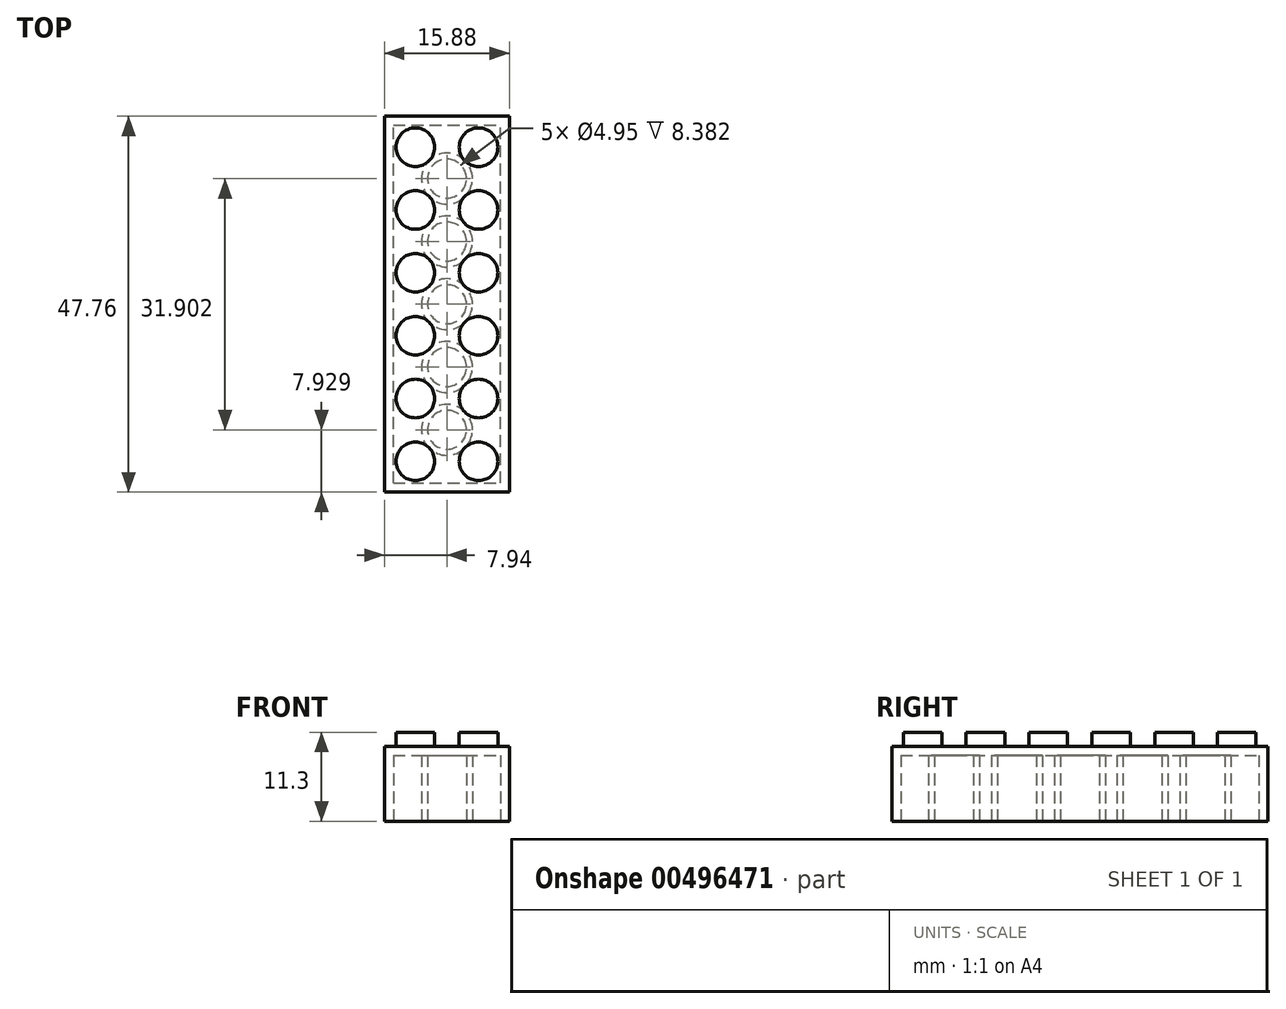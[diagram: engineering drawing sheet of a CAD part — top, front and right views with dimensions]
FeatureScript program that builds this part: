
annotation { "Feature Type Name" : "Feature", "Feature Type Description" : "" }
export const myFeature = defineFeature(function(context is Context, id is Id, definition is map)
    precondition{}
    {
        {
            var Q0;
            Q0=qCreatedBy(makeId("Top.planeOp"),FACE);
            var sketch = newSketch(context, id + "F0", { "sketchPlane" : qUnion([Q0])});
            skLineSegment(sketch, "E0.bottom", {"start": v(7.94, 23.88) * mm, "end": v(-7.94, 23.88) * mm});
            skLineSegment(sketch, "E0.top", {"start": v(7.94, -23.88) * mm, "end": v(-7.94, -23.88) * mm});
            skLineSegment(sketch, "E0.left", {"start": v(7.94, 23.88) * mm, "end": v(7.94, -23.88) * mm});
            skLineSegment(sketch, "E0.right", {"start": v(-7.94, 23.88) * mm, "end": v(-7.94, -23.88) * mm});
            skPoint(sketch, "E0.middle", {"position": v(0, 0) * mm});
            skSolve(sketch);
        }
        {
            var Q0;
            Q0=makeQuery(id+"F0.imprint","IMPRINT",FACE,{"disambiguationData":[TD([[makeQuery(id+"F0.imprint","IMPRINT",EDGE,{"derivedFrom":sQuery(id+"F0.wireOp",EDGE,"E0.bottom")}),1.0]])]});
            extrude(context, id + "F1", {"entities" : qUnion([Q0]), "endBound" : BoundingType.SYMMETRIC, "depth" : 9.52 * mm});
        }
        {
            var Q0;
            Q0=makeQuery(id+"F1.opExtrude","CAP_FACE",FACE,{"disambiguationData":[OSD([sQuery(id+"F0.wireOp",EDGE,"E0.bottom"),sQuery(id+"F0.wireOp",EDGE,"E0.top"),sQuery(id+"F0.wireOp",EDGE,"E0.left"),sQuery(id+"F0.wireOp",EDGE,"E0.right")])],"isStart":false});
            var sketch = newSketch(context, id + "F2", { "sketchPlane" : qUnion([Q0])});
            skCircle(sketch, "E1", {"center": v(-4.01, 19.95) * mm, "radius": 2.45 * mm});
            skCircle(sketch, "E2", {"center": v(4.01, 19.95) * mm, "radius": 2.45 * mm});
            skCircle(sketch, "E3", {"center": v(-4.01, -19.95) * mm, "radius": 2.45 * mm});
            skCircle(sketch, "E4", {"center": v(4.01, -19.95) * mm, "radius": 2.45 * mm});
            skCircle(sketch, "E5", {"center": v(4.01, -11.98) * mm, "radius": 2.45 * mm});
            skCircle(sketch, "E6", {"center": v(4.01, -4) * mm, "radius": 2.45 * mm});
            skCircle(sketch, "E7", {"center": v(-4.01, -11.98) * mm, "radius": 2.45 * mm});
            skCircle(sketch, "E8", {"center": v(-4.01, -4) * mm, "radius": 2.45 * mm});
            skCircle(sketch, "E9", {"center": v(-4.01, 11.98) * mm, "radius": 2.45 * mm});
            skCircle(sketch, "E10", {"center": v(4.01, 11.98) * mm, "radius": 2.45 * mm});
            skCircle(sketch, "E11", {"center": v(4.01, 4) * mm, "radius": 2.45 * mm});
            skCircle(sketch, "E12", {"center": v(-4.01, 4) * mm, "radius": 2.45 * mm});
            skSolve(sketch);
        }
        {
            var Q0;
            Q0=makeQuery(id+"F2.imprint","IMPRINT",FACE,{"disambiguationData":[TD([[makeQuery(id+"F2.imprint","IMPRINT",EDGE,{"derivedFrom":sQuery(id+"F2.wireOp",EDGE,"E1")}),1.0]])]});
            var Q1;
            Q1=makeQuery(id+"F2.imprint","IMPRINT",FACE,{"disambiguationData":[TD([[makeQuery(id+"F2.imprint","IMPRINT",EDGE,{"derivedFrom":sQuery(id+"F2.wireOp",EDGE,"E2")}),1.0]])]});
            var Q2;
            Q2=makeQuery(id+"F2.imprint","IMPRINT",FACE,{"disambiguationData":[TD([[makeQuery(id+"F2.imprint","IMPRINT",EDGE,{"derivedFrom":sQuery(id+"F2.wireOp",EDGE,"E9")}),1.0]])]});
            var Q3;
            Q3=makeQuery(id+"F2.imprint","IMPRINT",FACE,{"disambiguationData":[TD([[makeQuery(id+"F2.imprint","IMPRINT",EDGE,{"derivedFrom":sQuery(id+"F2.wireOp",EDGE,"E10")}),1.0]])]});
            var Q4;
            Q4=makeQuery(id+"F2.imprint","IMPRINT",FACE,{"disambiguationData":[TD([[makeQuery(id+"F2.imprint","IMPRINT",EDGE,{"derivedFrom":sQuery(id+"F2.wireOp",EDGE,"E11")}),1.0]])]});
            var Q5;
            Q5=makeQuery(id+"F2.imprint","IMPRINT",FACE,{"disambiguationData":[TD([[makeQuery(id+"F2.imprint","IMPRINT",EDGE,{"derivedFrom":sQuery(id+"F2.wireOp",EDGE,"E12")}),1.0]])]});
            var Q6;
            Q6=makeQuery(id+"F2.imprint","IMPRINT",FACE,{"disambiguationData":[TD([[makeQuery(id+"F2.imprint","IMPRINT",EDGE,{"derivedFrom":sQuery(id+"F2.wireOp",EDGE,"E8")}),1.0]])]});
            var Q7;
            Q7=makeQuery(id+"F2.imprint","IMPRINT",FACE,{"disambiguationData":[TD([[makeQuery(id+"F2.imprint","IMPRINT",EDGE,{"derivedFrom":sQuery(id+"F2.wireOp",EDGE,"E6")}),1.0]])]});
            var Q8;
            Q8=makeQuery(id+"F2.imprint","IMPRINT",FACE,{"disambiguationData":[TD([[makeQuery(id+"F2.imprint","IMPRINT",EDGE,{"derivedFrom":sQuery(id+"F2.wireOp",EDGE,"E5")}),1.0]])]});
            var Q9;
            Q9=makeQuery(id+"F2.imprint","IMPRINT",FACE,{"disambiguationData":[TD([[makeQuery(id+"F2.imprint","IMPRINT",EDGE,{"derivedFrom":sQuery(id+"F2.wireOp",EDGE,"E7")}),1.0]])]});
            var Q10;
            Q10=makeQuery(id+"F2.imprint","IMPRINT",FACE,{"disambiguationData":[TD([[makeQuery(id+"F2.imprint","IMPRINT",EDGE,{"derivedFrom":sQuery(id+"F2.wireOp",EDGE,"E3")}),1.0]])]});
            var Q11;
            Q11=makeQuery(id+"F2.imprint","IMPRINT",FACE,{"disambiguationData":[TD([[makeQuery(id+"F2.imprint","IMPRINT",EDGE,{"derivedFrom":sQuery(id+"F2.wireOp",EDGE,"E4")}),1.0]])]});
            extrude(context, id + "F3", {"entities" : qUnion([Q0, Q1, Q2, Q3, Q4, Q5, Q6, Q7, Q8, Q9, Q10, Q11]), "operationType" : NewBodyOperationType.ADD, "depth" : 1.78 * mm});
        }
        {
            var Q0;
            Q0=makeQuery(id+"F1.opExtrude","CAP_FACE",FACE,{"disambiguationData":[OSD([sQuery(id+"F0.wireOp",EDGE,"E0.bottom"),sQuery(id+"F0.wireOp",EDGE,"E0.top"),sQuery(id+"F0.wireOp",EDGE,"E0.left"),sQuery(id+"F0.wireOp",EDGE,"E0.right")])],"isStart":true});
            var sketch = newSketch(context, id + "F4", { "sketchPlane" : qUnion([Q0])});
            skLineSegment(sketch, "E13.bottom", {"start": v(-6.8, 22.73) * mm, "end": v(6.8, 22.73) * mm});
            skLineSegment(sketch, "E13.top", {"start": v(-6.8, -22.73) * mm, "end": v(6.8, -22.73) * mm});
            skLineSegment(sketch, "E13.left", {"start": v(-6.8, 22.73) * mm, "end": v(-6.8, -22.73) * mm});
            skLineSegment(sketch, "E13.right", {"start": v(6.8, 22.73) * mm, "end": v(6.8, -22.73) * mm});
            skPoint(sketch, "E13.middle", {"position": v(0, 0) * mm});
            skCircle(sketch, "E14", {"center": v(0, 0) * mm, "radius": 3.24 * mm});
            skCircle(sketch, "E15", {"center": v(0, 7.98) * mm, "radius": 3.24 * mm});
            skCircle(sketch, "E16", {"center": v(0, 15.95) * mm, "radius": 3.24 * mm});
            skCircle(sketch, "E17", {"center": v(0, -7.98) * mm, "radius": 3.24 * mm});
            skCircle(sketch, "E18", {"center": v(0, -15.95) * mm, "radius": 3.24 * mm});
            skSolve(sketch);
        }
        {
            var Q0;
            Q0=makeQuery(id+"F4.imprint","IMPRINT",FACE,{"disambiguationData":[TD([[makeQuery(id+"F4.imprint","IMPRINT",EDGE,{"derivedFrom":sQuery(id+"F4.wireOp",EDGE,"E13.bottom")}),-1.0]])]});
            extrude(context, id + "F5", {"entities" : qUnion([Q0]), "operationType" : NewBodyOperationType.REMOVE, "oppositeDirection" : true, "depth" : 8.38 * mm});
        }
        {
            var Q0;
            Q0=makeQuery(id+"F5.boolean.opBoolean","SPLIT",FACE,{"disambiguationData":[TD([makeQuery(id+"F5.opExtrude","SWEPT_FACE",FACE,{"disambiguationData":[OSD([sQuery(id+"F4.wireOp",EDGE,"E14")])]})])],"derivedFrom":makeQuery(id+"F1.opExtrude","CAP_FACE",FACE,{"disambiguationData":[OSD([sQuery(id+"F0.wireOp",EDGE,"E0.bottom"),sQuery(id+"F0.wireOp",EDGE,"E0.top"),sQuery(id+"F0.wireOp",EDGE,"E0.left"),sQuery(id+"F0.wireOp",EDGE,"E0.right")])],"isStart":true})});
            var sketch = newSketch(context, id + "F6", { "sketchPlane" : qUnion([Q0])});
            skCircle(sketch, "E19", {"center": v(0, 0) * mm, "radius": 2.48 * mm});
            skSolve(sketch);
        }
        {
            var Q0;
            Q0=makeQuery(id+"F5.boolean.opBoolean","SPLIT",FACE,{"disambiguationData":[TD([makeQuery(id+"F5.opExtrude","SWEPT_FACE",FACE,{"disambiguationData":[OSD([sQuery(id+"F4.wireOp",EDGE,"E15")])]})])],"derivedFrom":makeQuery(id+"F1.opExtrude","CAP_FACE",FACE,{"disambiguationData":[OSD([sQuery(id+"F0.wireOp",EDGE,"E0.bottom"),sQuery(id+"F0.wireOp",EDGE,"E0.top"),sQuery(id+"F0.wireOp",EDGE,"E0.left"),sQuery(id+"F0.wireOp",EDGE,"E0.right")])],"isStart":true})});
            var sketch = newSketch(context, id + "F7", { "sketchPlane" : qUnion([Q0])});
            skCircle(sketch, "E20", {"center": v(0, 7.98) * mm, "radius": 2.48 * mm});
            skSolve(sketch);
        }
        {
            var Q0;
            Q0=makeQuery(id+"F5.boolean.opBoolean","SPLIT",FACE,{"disambiguationData":[TD([makeQuery(id+"F5.opExtrude","SWEPT_FACE",FACE,{"disambiguationData":[OSD([sQuery(id+"F4.wireOp",EDGE,"E16")])]})])],"derivedFrom":makeQuery(id+"F1.opExtrude","CAP_FACE",FACE,{"disambiguationData":[OSD([sQuery(id+"F0.wireOp",EDGE,"E0.bottom"),sQuery(id+"F0.wireOp",EDGE,"E0.top"),sQuery(id+"F0.wireOp",EDGE,"E0.left"),sQuery(id+"F0.wireOp",EDGE,"E0.right")])],"isStart":true})});
            var sketch = newSketch(context, id + "F8", { "sketchPlane" : qUnion([Q0])});
            skCircle(sketch, "E21", {"center": v(0, 15.95) * mm, "radius": 2.48 * mm});
            skSolve(sketch);
        }
        {
            var Q0;
            Q0=makeQuery(id+"F5.boolean.opBoolean","SPLIT",FACE,{"disambiguationData":[TD([makeQuery(id+"F5.opExtrude","SWEPT_FACE",FACE,{"disambiguationData":[OSD([sQuery(id+"F4.wireOp",EDGE,"E17")])]})])],"derivedFrom":makeQuery(id+"F1.opExtrude","CAP_FACE",FACE,{"disambiguationData":[OSD([sQuery(id+"F0.wireOp",EDGE,"E0.bottom"),sQuery(id+"F0.wireOp",EDGE,"E0.top"),sQuery(id+"F0.wireOp",EDGE,"E0.left"),sQuery(id+"F0.wireOp",EDGE,"E0.right")])],"isStart":true})});
            var sketch = newSketch(context, id + "F9", { "sketchPlane" : qUnion([Q0])});
            skCircle(sketch, "E22", {"center": v(0, -7.98) * mm, "radius": 2.48 * mm});
            skSolve(sketch);
        }
        {
            var Q0;
            Q0=makeQuery(id+"F5.boolean.opBoolean","SPLIT",FACE,{"disambiguationData":[TD([makeQuery(id+"F5.opExtrude","SWEPT_FACE",FACE,{"disambiguationData":[OSD([sQuery(id+"F4.wireOp",EDGE,"E18")])]})])],"derivedFrom":makeQuery(id+"F1.opExtrude","CAP_FACE",FACE,{"disambiguationData":[OSD([sQuery(id+"F0.wireOp",EDGE,"E0.bottom"),sQuery(id+"F0.wireOp",EDGE,"E0.top"),sQuery(id+"F0.wireOp",EDGE,"E0.left"),sQuery(id+"F0.wireOp",EDGE,"E0.right")])],"isStart":true})});
            var sketch = newSketch(context, id + "F10", { "sketchPlane" : qUnion([Q0])});
            skCircle(sketch, "E23", {"center": v(0, -15.95) * mm, "radius": 2.48 * mm});
            skSolve(sketch);
        }
        {
            var Q0;
            Q0=makeQuery(id+"F8.imprint","IMPRINT",FACE,{"disambiguationData":[TD([[makeQuery(id+"F8.imprint","IMPRINT",EDGE,{"derivedFrom":sQuery(id+"F8.wireOp",EDGE,"E21")}),1.0]])]});
            var Q1;
            Q1=makeQuery(id+"F7.imprint","IMPRINT",FACE,{"disambiguationData":[TD([[makeQuery(id+"F7.imprint","IMPRINT",EDGE,{"derivedFrom":sQuery(id+"F7.wireOp",EDGE,"E20")}),1.0]])]});
            var Q2;
            Q2=makeQuery(id+"F6.imprint","IMPRINT",FACE,{"disambiguationData":[TD([[makeQuery(id+"F6.imprint","IMPRINT",EDGE,{"derivedFrom":sQuery(id+"F6.wireOp",EDGE,"E19")}),1.0]])]});
            var Q3;
            Q3=makeQuery(id+"F9.imprint","IMPRINT",FACE,{"disambiguationData":[TD([[makeQuery(id+"F9.imprint","IMPRINT",EDGE,{"derivedFrom":sQuery(id+"F9.wireOp",EDGE,"E22")}),1.0]])]});
            var Q4;
            Q4=makeQuery(id+"F10.imprint","IMPRINT",FACE,{"disambiguationData":[TD([[makeQuery(id+"F10.imprint","IMPRINT",EDGE,{"derivedFrom":sQuery(id+"F10.wireOp",EDGE,"E23")}),1.0]])]});
            extrude(context, id + "F11", {"entities" : qUnion([Q0, Q1, Q2, Q3, Q4]), "operationType" : NewBodyOperationType.REMOVE, "oppositeDirection" : true, "depth" : 8.38 * mm});
        }
    });
